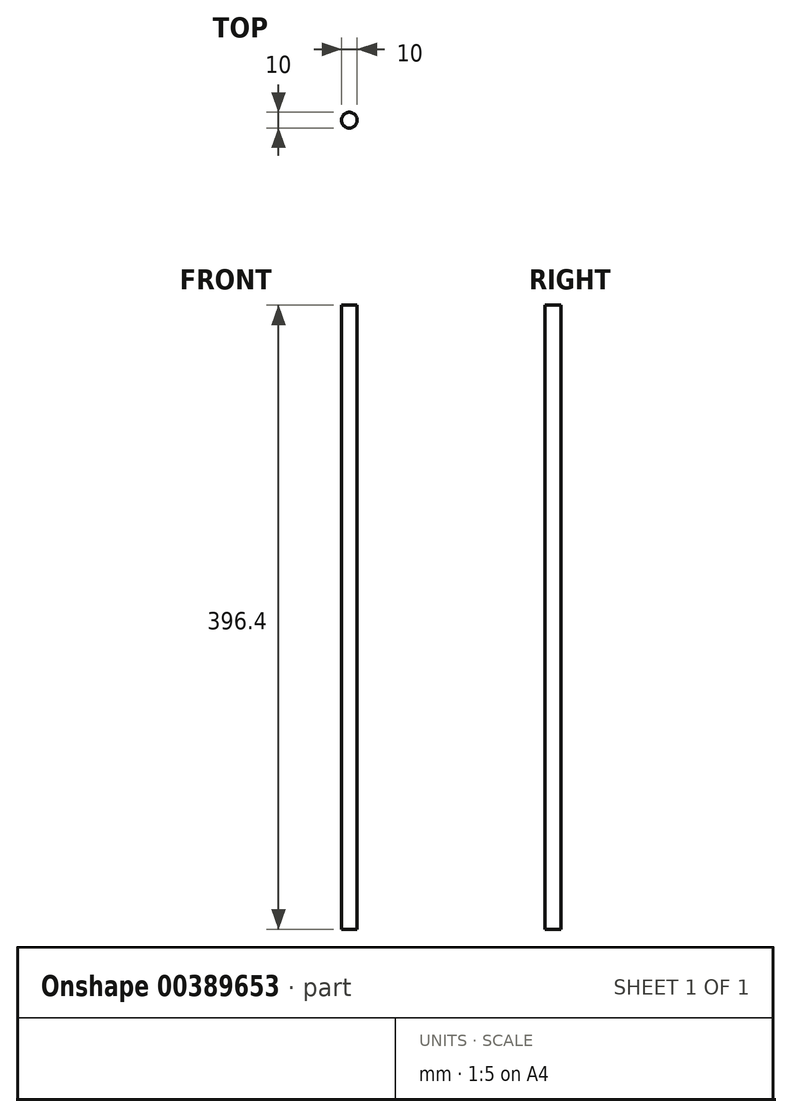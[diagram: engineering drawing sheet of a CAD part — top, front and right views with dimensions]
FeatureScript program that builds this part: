
annotation { "Feature Type Name" : "Feature", "Feature Type Description" : "" }
export const myFeature = defineFeature(function(context is Context, id is Id, definition is map)
    precondition{}
    {
        {
            var Q0;
            Q0=qCreatedBy(makeId("Top.planeOp"),FACE);
            var sketch = newSketch(context, id + "F0", { "sketchPlane" : qUnion([Q0])});
            skCircle(sketch, "E0", {"center": v(0, 0) * mm, "radius": 5 * mm});
            skSolve(sketch);
        }
        {
            var Q0;
            Q0=qSketchRegion(id+"F0",true);
            extrude(context, id + "F1", {"entities" : qUnion([Q0]), "depth" : 396.4 * mm});
        }
    });
